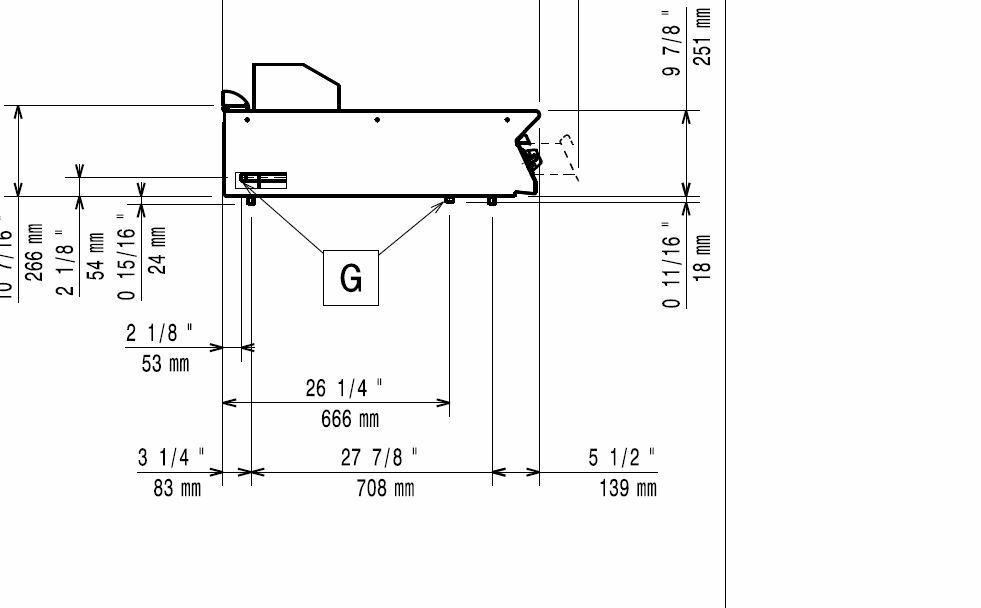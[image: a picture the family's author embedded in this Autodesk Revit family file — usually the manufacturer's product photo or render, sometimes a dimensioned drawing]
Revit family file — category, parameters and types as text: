
# Revit family: QF_ELECTROLUXPROFESSIONAL_391590_E9IINTAOMEI
name_source: partatom
category: Attrezzature speciali
revit_build: Autodesk Revit 2018 (Build: 20181011_1500(x64)
units: mm (PartAtom-declared; Revit-internal decimal feet)

## family parameters
Basato su piano di lavoro = No
Condiviso = No
Punto di calcolo locali = No
Quota connettore circolare = Usa diametro
Sempre verticale = Sì
Taglio con vuoti quando caricato = No
Tipo di parte = Normale

## types (1)
- Standard
    Accessory = Sì
    Cold Water Size = 0"
    Compressed Air Pressure = 0.00 psi
    Compressed Air Size = 0"
    Compressed Air Volume = 0 GPM
    Condensate Return Size = 0"
    Cycle = 0 Hz
    Depth Actual = 930 mm
    Descrizione = GAS FRY TOP SMOOTH HORIZONTAL 800MM-BRUSHED CHROME - QMARK
    Direct Waste Size = 0"
    Gas Input Pressure = 0.7
    Gas KW = 20
    Gas Size = 1"
    HP = 0 HP
    Height Actual = 250 mm  [stored 0.82021 ft]
    Hot Water Size = 0"
    Item Number = 391590
    Length Actual = 800 mm  [stored 2.62467 ft]
    Modello = E9IINTAOMEI
    Phase = 0
    Produttore = Electrolux Professional
    Refrigerant Compressor Remote = Sì
    Refrigeration Liquid Line Size = 0 mm  [stored 0 ft]
    Refrigeration Suction Line Size = 0 mm  [stored 0 ft]
    Steam Consumption per Hour = 0
    Steam Supply Maximum Pressure = 0.00 psi
    Steam Supply Minimum Pressure = 0.00 psi
    Steam Supply Size = 0"
    URL = https://www.electroluxprofessional.com
    URL Manufacturer = https://www.electroluxprofessional.com
    Volts = 0 V
    Watts = 0 W
    Weight = 105.00 kg

note: source unit labels omitted for Gas Input Pressure — the stored unit's dimension contradicts the parameter name (converter mislabeling)

note: [stored X ft] marks values corroborated as IEEE doubles in the binary element streams (Revit-internal decimal feet)

## geometry (parser evidence)
native form markers: Blend x28, Sweep x2
no freeform markers — native parametric forms only
